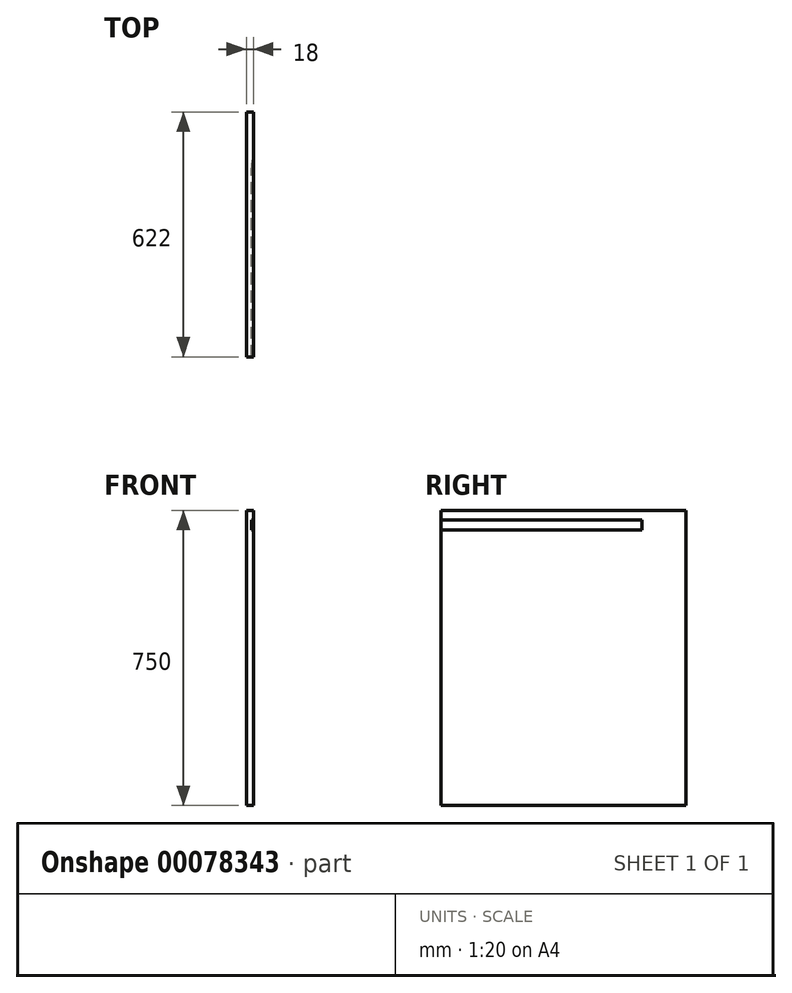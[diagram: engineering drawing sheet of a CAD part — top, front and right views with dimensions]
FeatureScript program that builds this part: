
annotation { "Feature Type Name" : "Feature", "Feature Type Description" : "" }
export const myFeature = defineFeature(function(context is Context, id is Id, definition is map)
    precondition{}
    {
        {
            var Q0;
            Q0=qCreatedBy(makeId("Right.planeOp"),FACE);
            var sketch = newSketch(context, id + "F0", { "sketchPlane" : qUnion([Q0])});
            skLineSegment(sketch, "E0.bottom", {"start": v(-308.23, 451.19) * mm, "end": v(313.77, 451.19) * mm});
            skLineSegment(sketch, "E0.top", {"start": v(-308.23, -298.81) * mm, "end": v(313.77, -298.81) * mm});
            skLineSegment(sketch, "E0.left", {"start": v(-308.23, 451.19) * mm, "end": v(-308.23, -298.81) * mm});
            skLineSegment(sketch, "E0.right", {"start": v(313.77, 451.19) * mm, "end": v(313.77, -298.81) * mm});
            skSolve(sketch);
        }
        {
            var Q0;
            Q0=makeQuery(id+"F0.imprint","IMPRINT",FACE,{"disambiguationData":[TD([[makeQuery(id+"F0.imprint","IMPRINT",EDGE,{"derivedFrom":sQuery(id+"F0.wireOp",EDGE,"E0.bottom")}),-1.0]])]});
            extrude(context, id + "F1", {"entities" : qUnion([Q0]), "depth" : 18 * mm});
        }
        {
            var Q0;
            Q0=makeQuery(id+"F1.opExtrude","SWEPT_FACE",FACE,{"disambiguationData":[OSD([sQuery(id+"F0.wireOp",EDGE,"E0.bottom")])]});
            cPlane(context, id + "F2", {"entities" : qUnion([Q0]), "cplaneType" : CPlaneType.OFFSET, "offset" : 25 * mm, "oppositeDirection" : true, "width" : 150 * mm, "height" : 150 * mm});
        }
        {
            var Q0;
            Q0=qCreatedBy(id+"F2.planeOp",FACE);
            var sketch = newSketch(context, id + "F3", { "sketchPlane" : qUnion([Q0])});
            skLineSegment(sketch, "E1", {"start": v(5, -308.23) * mm, "end": v(5, 171.77) * mm});
            skPoint(sketch, "E2.visualSharp", {"position": v(5, 203.4) * mm});
            skArc(sketch, "E3", {"start": v(5, 171.77) * mm, "mid": v(3.74, 186.97) * mm, "end": v(0, 201.77) * mm});
            skLineSegment(sketch, "E4", {"start": v(0, 201.77) * mm, "end": v(0, -308.23) * mm});
            skLineSegment(sketch, "E5", {"start": v(0, -308.23) * mm, "end": v(5, -308.23) * mm});
            skSolve(sketch);
        }
        {
            var Q0;
            {var subQ0=sQuery(id+"F3.wireOp",EDGE,"E1");Q0=makeQuery(id+"F3.imprint","IMPRINT",FACE,{"disambiguationData":[TD([[makeQuery(id+"F3.imprint","IMPRINT",EDGE,{"derivedFrom":subQ0}),1.0]])]});}
            extrude(context, id + "F4", {"entities" : qUnion([Q0]), "operationType" : NewBodyOperationType.REMOVE, "oppositeDirection" : true, "depth" : 25 * mm});
        }
        {
            var Q0;
            Q0=makeQuery(id+"F1.opExtrude","SWEPT_BODY",BODY,{"disambiguationData":[OSD([sQuery(id+"F0.wireOp",EDGE,"E0.bottom"),sQuery(id+"F0.wireOp",EDGE,"E0.top"),sQuery(id+"F0.wireOp",EDGE,"E0.left"),sQuery(id+"F0.wireOp",EDGE,"E0.right")])]});
            var Q1;
            Q1=qCreatedBy(makeId("Right.planeOp"),FACE);
            mirror(context, id + "F5", {"entities" : qUnion([Q0]), "mirrorPlane" : qUnion([Q1])});
        }
        {
            var Q0;
            Q0=makeQuery(id+"F1.opExtrude","SWEPT_BODY",BODY,{"disambiguationData":[OSD([sQuery(id+"F0.wireOp",EDGE,"E0.bottom"),sQuery(id+"F0.wireOp",EDGE,"E0.top"),sQuery(id+"F0.wireOp",EDGE,"E0.left"),sQuery(id+"F0.wireOp",EDGE,"E0.right")])]});
            deleteBodies(context, id + "F6", {"entities" : qUnion([Q0])});
        }
    });
